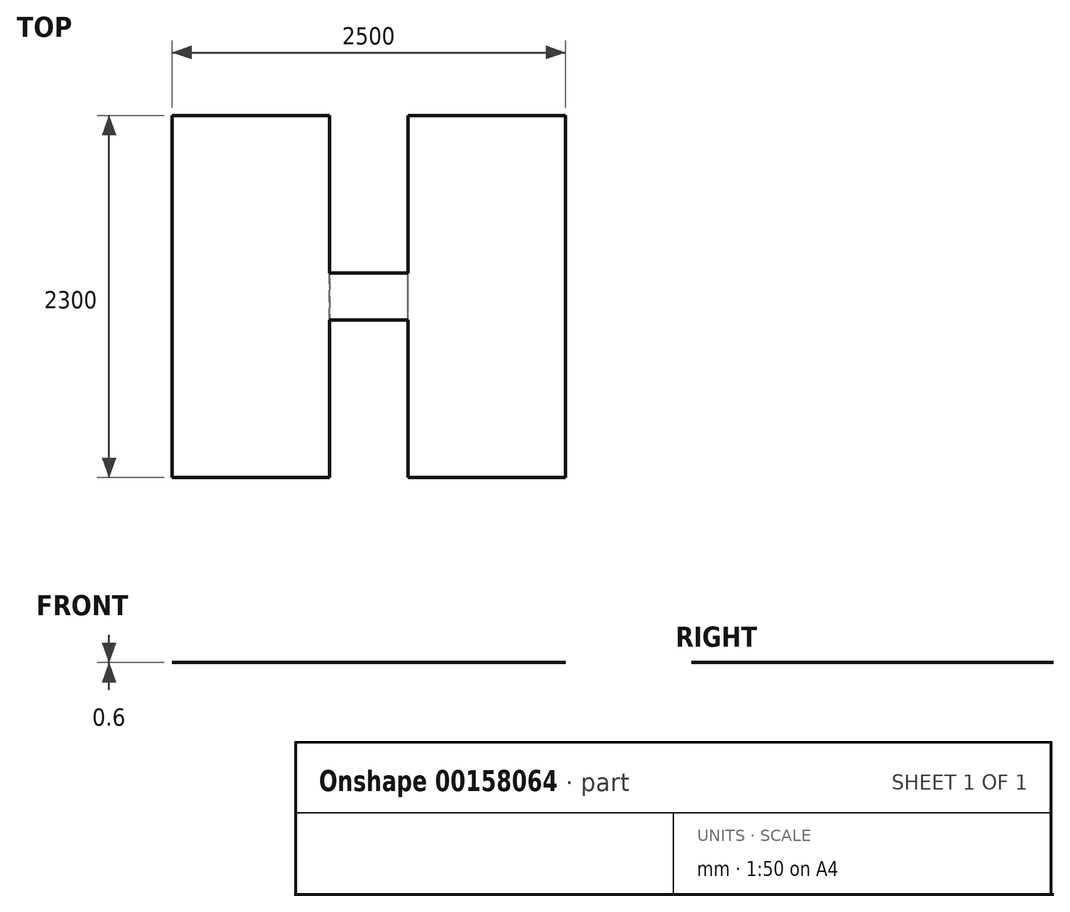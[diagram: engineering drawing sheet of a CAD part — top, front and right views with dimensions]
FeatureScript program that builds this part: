
annotation { "Feature Type Name" : "Feature", "Feature Type Description" : "" }
export const myFeature = defineFeature(function(context is Context, id is Id, definition is map)
    precondition{}
    {
        {
            var Q0;
            Q0=qCreatedBy(makeId("Right.planeOp"),FACE);
            var sketch = newSketch(context, id + "F0", { "sketchPlane" : qUnion([Q0])});
            skLineSegment(sketch, "E0.bottom", {"start": v(0, 0) * mm, "end": v(300, 0) * mm});
            skLineSegment(sketch, "E0.top", {"start": v(0, 0.1) * mm, "end": v(300, 0.1) * mm});
            skLineSegment(sketch, "E0.left", {"start": v(0, 0) * mm, "end": v(0, 0.1) * mm});
            skLineSegment(sketch, "E0.right", {"start": v(300, 0) * mm, "end": v(300, 0.1) * mm});
            skSolve(sketch);
        }
        {
            var Q0;
            Q0=qSketchRegion(id+"F0",true);
            extrude(context, id + "F1", {"entities" : qUnion([Q0]), "endBound" : BoundingType.SYMMETRIC, "depth" : 500 * mm});
        }
        {
            var Q0;
            Q0=makeQuery(id+"F1.opExtrude","CAP_FACE",FACE,{"disambiguationData":[OSD([sQuery(id+"F0.wireOp",EDGE,"E0.bottom"),sQuery(id+"F0.wireOp",EDGE,"E0.top"),sQuery(id+"F0.wireOp",EDGE,"E0.left"),sQuery(id+"F0.wireOp",EDGE,"E0.right")])],"isStart":false});
            var sketch = newSketch(context, id + "F2", { "sketchPlane" : qUnion([Q0])});
            skLineSegment(sketch, "E1.bottom", {"start": v(0, 0.1) * mm, "end": v(300, 0.1) * mm});
            skLineSegment(sketch, "E1.top", {"start": v(0, -0.5) * mm, "end": v(300, -0.5) * mm});
            skLineSegment(sketch, "E1.left", {"start": v(0, 0.1) * mm, "end": v(0, -0.5) * mm});
            skLineSegment(sketch, "E1.right", {"start": v(300, 0.1) * mm, "end": v(300, -0.5) * mm});
            skSolve(sketch);
        }
        {
            var Q0;
            Q0=qSketchRegion(id+"F2",true);
            extrude(context, id + "F3", {"entities" : qUnion([Q0]), "operationType" : NewBodyOperationType.ADD, "depth" : 1000 * mm});
        }
        {
            var Q0;
            Q0=makeQuery(id+"F1.opExtrude","CAP_FACE",FACE,{"disambiguationData":[OSD([sQuery(id+"F0.wireOp",EDGE,"E0.bottom"),sQuery(id+"F0.wireOp",EDGE,"E0.top"),sQuery(id+"F0.wireOp",EDGE,"E0.left"),sQuery(id+"F0.wireOp",EDGE,"E0.right")])],"isStart":true});
            var sketch = newSketch(context, id + "F4", { "sketchPlane" : qUnion([Q0])});
            skLineSegment(sketch, "E2.bottom", {"start": v(-300, 0.1) * mm, "end": v(0, 0.1) * mm});
            skLineSegment(sketch, "E2.top", {"start": v(-300, -0.5) * mm, "end": v(0, -0.5) * mm});
            skLineSegment(sketch, "E2.left", {"start": v(-300, 0.1) * mm, "end": v(-300, -0.5) * mm});
            skLineSegment(sketch, "E2.right", {"start": v(0, 0.1) * mm, "end": v(0, -0.5) * mm});
            skSolve(sketch);
        }
        {
            var Q0;
            Q0=qSketchRegion(id+"F4",true);
            extrude(context, id + "F5", {"entities" : qUnion([Q0]), "operationType" : NewBodyOperationType.ADD, "depth" : 1000 * mm});
        }
        {
            var Q0;
            Q0=makeQuery(id+"F5.boolean.opBoolean","MERGE",FACE,{"derivedFrom":[makeQuery(id+"F3.boolean.opBoolean","MERGE",FACE,{"derivedFrom":[makeQuery(id+"F1.opExtrude","SWEPT_FACE",FACE,{"disambiguationData":[OSD([sQuery(id+"F0.wireOp",EDGE,"E0.right")])]}),makeQuery(id+"F3.opExtrude","SWEPT_FACE",FACE,{"disambiguationData":[OSD([sQuery(id+"F2.wireOp",EDGE,"E1.right")])]})]}),makeQuery(id+"F5.opExtrude","SWEPT_FACE",FACE,{"disambiguationData":[OSD([sQuery(id+"F4.wireOp",EDGE,"E2.left")])]})]});
            var sketch = newSketch(context, id + "F6", { "sketchPlane" : qUnion([Q0])});
            skLineSegment(sketch, "E3.bottom", {"start": v(-250, -0.5) * mm, "end": v(-1250, -0.5) * mm});
            skLineSegment(sketch, "E3.top", {"start": v(-250, 0.1) * mm, "end": v(-1250, 0.1) * mm});
            skLineSegment(sketch, "E3.left", {"start": v(-250, -0.5) * mm, "end": v(-250, 0.1) * mm});
            skLineSegment(sketch, "E3.right", {"start": v(-1250, -0.5) * mm, "end": v(-1250, 0.1) * mm});
            skLineSegment(sketch, "E4.bottom", {"start": v(250, -0.5) * mm, "end": v(1250, -0.5) * mm});
            skLineSegment(sketch, "E4.top", {"start": v(250, 0.1) * mm, "end": v(1250, 0.1) * mm});
            skLineSegment(sketch, "E4.left", {"start": v(250, -0.5) * mm, "end": v(250, 0.1) * mm});
            skLineSegment(sketch, "E4.right", {"start": v(1250, -0.5) * mm, "end": v(1250, 0.1) * mm});
            skSolve(sketch);
        }
        {
            var Q0;
            Q0=qSketchRegion(id+"F6",true);
            extrude(context, id + "F7", {"entities" : qUnion([Q0]), "operationType" : NewBodyOperationType.ADD, "depth" : 1000 * mm});
        }
        {
            var Q0;
            Q0=makeQuery(id+"F5.boolean.opBoolean","MERGE",FACE,{"derivedFrom":[makeQuery(id+"F3.boolean.opBoolean","MERGE",FACE,{"derivedFrom":[makeQuery(id+"F1.opExtrude","SWEPT_FACE",FACE,{"disambiguationData":[OSD([sQuery(id+"F0.wireOp",EDGE,"E0.left")])]}),makeQuery(id+"F3.opExtrude","SWEPT_FACE",FACE,{"disambiguationData":[OSD([sQuery(id+"F2.wireOp",EDGE,"E1.left")])]})]}),makeQuery(id+"F5.opExtrude","SWEPT_FACE",FACE,{"disambiguationData":[OSD([sQuery(id+"F4.wireOp",EDGE,"E2.right")])]})]});
            var sketch = newSketch(context, id + "F8", { "sketchPlane" : qUnion([Q0])});
            skLineSegment(sketch, "E5.bottom", {"start": v(-250, -0.5) * mm, "end": v(-1250, -0.5) * mm});
            skLineSegment(sketch, "E5.top", {"start": v(-250, 0.1) * mm, "end": v(-1250, 0.1) * mm});
            skLineSegment(sketch, "E5.left", {"start": v(-250, -0.5) * mm, "end": v(-250, 0.1) * mm});
            skLineSegment(sketch, "E5.right", {"start": v(-1250, -0.5) * mm, "end": v(-1250, 0.1) * mm});
            skLineSegment(sketch, "E6.bottom", {"start": v(1250, 0.1) * mm, "end": v(250, 0.1) * mm});
            skLineSegment(sketch, "E6.top", {"start": v(1250, -0.5) * mm, "end": v(250, -0.5) * mm});
            skLineSegment(sketch, "E6.left", {"start": v(1250, 0.1) * mm, "end": v(1250, -0.5) * mm});
            skLineSegment(sketch, "E6.right", {"start": v(250, 0.1) * mm, "end": v(250, -0.5) * mm});
            skSolve(sketch);
        }
        {
            var Q0;
            Q0=qSketchRegion(id+"F8",true);
            extrude(context, id + "F9", {"entities" : qUnion([Q0]), "operationType" : NewBodyOperationType.ADD, "depth" : 1000 * mm});
        }
    });
